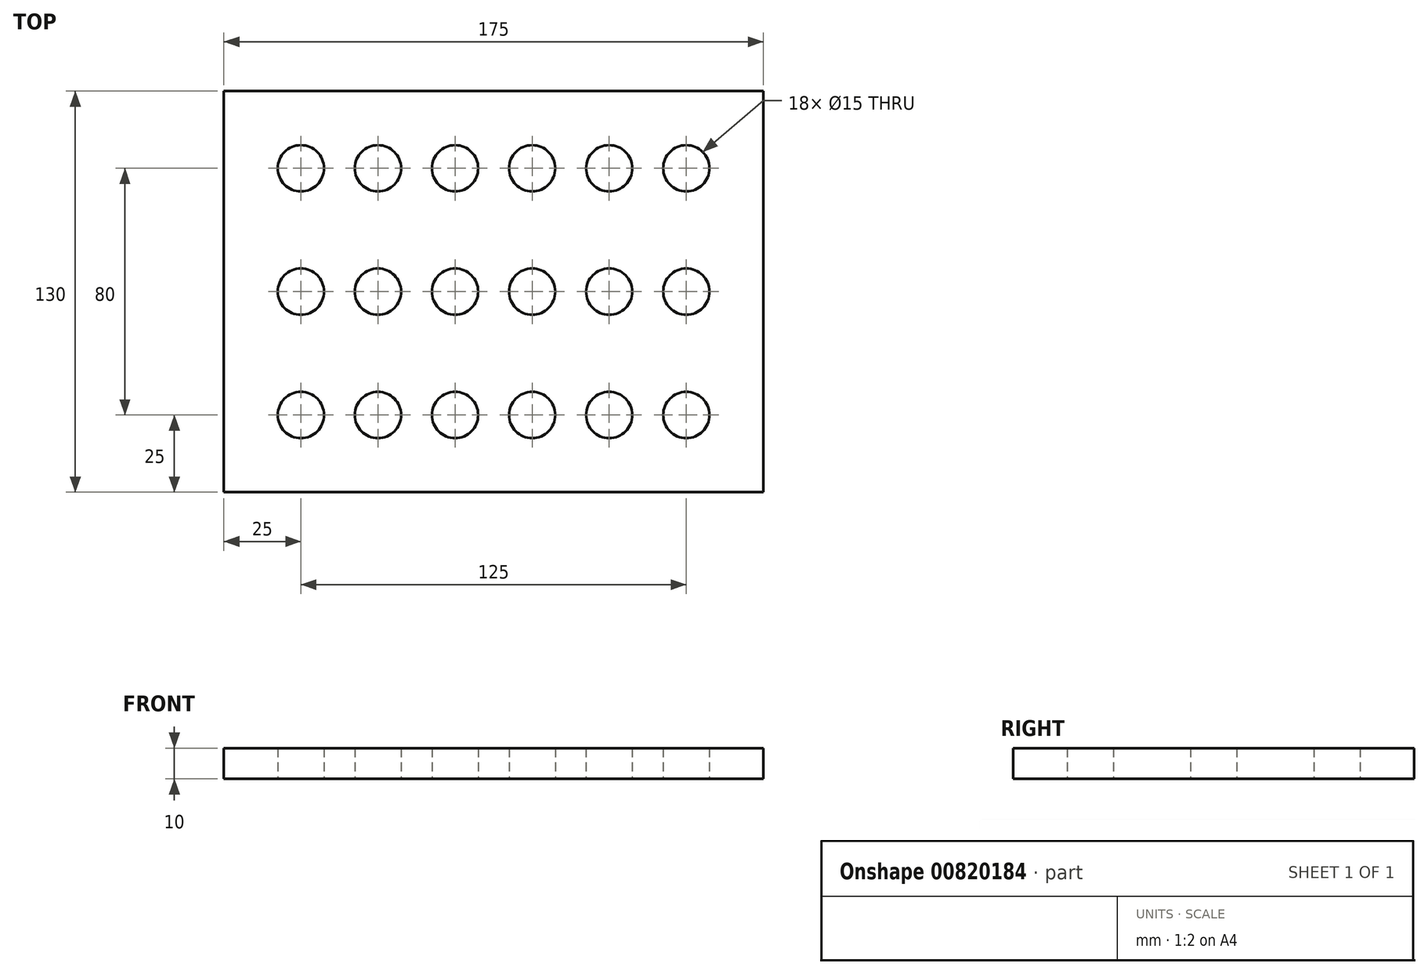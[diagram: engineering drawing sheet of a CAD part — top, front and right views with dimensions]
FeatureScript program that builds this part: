
annotation { "Feature Type Name" : "Feature", "Feature Type Description" : "" }
export const myFeature = defineFeature(function(context is Context, id is Id, definition is map)
    precondition{}
    {
        {
            var Q0;
            Q0=qCreatedBy(makeId("Top.planeOp"),FACE);
            var sketch = newSketch(context, id + "F0", { "sketchPlane" : qUnion([Q0])});
            skLineSegment(sketch, "E0.bottom", {"start": v(-87.5, -65) * mm, "end": v(87.5, -65) * mm});
            skLineSegment(sketch, "E0.top", {"start": v(-87.5, 65) * mm, "end": v(87.5, 65) * mm});
            skLineSegment(sketch, "E0.left", {"start": v(-87.5, -65) * mm, "end": v(-87.5, 65) * mm});
            skLineSegment(sketch, "E0.right", {"start": v(87.5, -65) * mm, "end": v(87.5, 65) * mm});
            skPoint(sketch, "E0.middle", {"position": v(0, 0) * mm});
            skCircle(sketch, "E1", {"center": v(-62.5, 40) * mm, "radius": 7.5 * mm});
            skLineSegment(sketch, "E2", {"start": v(-62.5, 40) * mm, "end": v(-87.5, 40) * mm});
            skLineSegment(sketch, "E3", {"start": v(-62.5, 40) * mm, "end": v(-62.5, 65) * mm, "construction": true});
            skCircle(sketch, "E4.0.1.0", {"center": v(-62.5, 0) * mm, "radius": 7.5 * mm});
            skCircle(sketch, "E4.0.2.0", {"center": v(-62.5, -40) * mm, "radius": 7.5 * mm});
            skCircle(sketch, "E4.1.0.0", {"center": v(-37.5, 40) * mm, "radius": 7.5 * mm});
            skCircle(sketch, "E4.1.1.0", {"center": v(-37.5, 0) * mm, "radius": 7.5 * mm});
            skCircle(sketch, "E4.1.2.0", {"center": v(-37.5, -40) * mm, "radius": 7.5 * mm});
            skCircle(sketch, "E4.2.0.0", {"center": v(-12.5, 40) * mm, "radius": 7.5 * mm});
            skCircle(sketch, "E4.2.1.0", {"center": v(-12.5, 0) * mm, "radius": 7.5 * mm});
            skCircle(sketch, "E4.2.2.0", {"center": v(-12.5, -40) * mm, "radius": 7.5 * mm});
            skCircle(sketch, "E4.3.0.0", {"center": v(12.5, 40) * mm, "radius": 7.5 * mm});
            skCircle(sketch, "E4.3.1.0", {"center": v(12.5, 0) * mm, "radius": 7.5 * mm});
            skCircle(sketch, "E4.3.2.0", {"center": v(12.5, -40) * mm, "radius": 7.5 * mm});
            skCircle(sketch, "E4.4.0.0", {"center": v(37.5, 40) * mm, "radius": 7.5 * mm});
            skCircle(sketch, "E4.4.1.0", {"center": v(37.5, 0) * mm, "radius": 7.5 * mm});
            skCircle(sketch, "E4.4.2.0", {"center": v(37.5, -40) * mm, "radius": 7.5 * mm});
            skCircle(sketch, "E4.5.0.0", {"center": v(62.5, 40) * mm, "radius": 7.5 * mm});
            skCircle(sketch, "E4.5.1.0", {"center": v(62.5, 0) * mm, "radius": 7.5 * mm});
            skCircle(sketch, "E4.5.2.0", {"center": v(62.5, -40) * mm, "radius": 7.5 * mm});
            skLineSegment(sketch, "E4.direction1", {"start": v(-62.5, 40) * mm, "end": v(-37.5, 40) * mm, "construction": true});
            skLineSegment(sketch, "E4.direction2", {"start": v(-62.5, 40) * mm, "end": v(-62.5, 0) * mm, "construction": true});
            skSolve(sketch);
        }
        {
            var Q0;
            Q0 = qSketchRegion(id + "F0", true);
            extrude(context, id + "F1", {"entities" : qUnion([Q0]), "depth" : 10 * mm, "offsetDistance" : 25.4 * mm});
        }
    });
